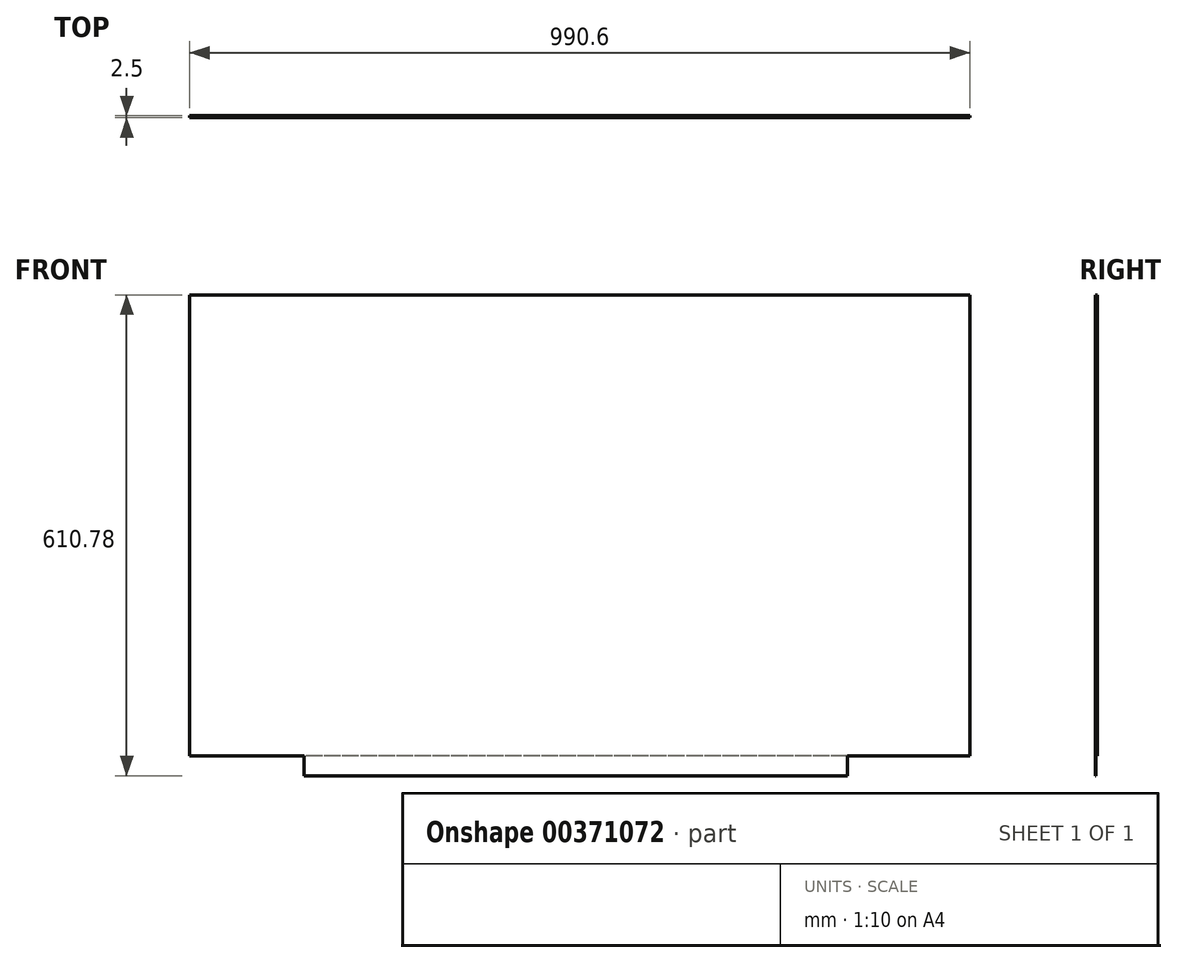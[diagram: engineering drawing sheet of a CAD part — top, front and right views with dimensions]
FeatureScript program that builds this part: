
annotation { "Feature Type Name" : "Feature", "Feature Type Description" : "" }
export const myFeature = defineFeature(function(context is Context, id is Id, definition is map)
    precondition{}
    {
        {
            var Q0;
            Q0=qCreatedBy(makeId("Front.planeOp"),FACE);
            var sketch = newSketch(context, id + "F0", { "sketchPlane" : qUnion([Q0])});
            skLineSegment(sketch, "E0.bottom", {"start": v(495.3, 292.9) * mm, "end": v(-495.3, 292.9) * mm});
            skLineSegment(sketch, "E0.top", {"start": v(495.3, -292.9) * mm, "end": v(-495.3, -292.9) * mm});
            skLineSegment(sketch, "E0.left", {"start": v(495.3, 292.9) * mm, "end": v(495.3, -292.9) * mm});
            skLineSegment(sketch, "E0.right", {"start": v(-495.3, 292.9) * mm, "end": v(-495.3, -292.9) * mm});
            skPoint(sketch, "E0.middle", {"position": v(0, 0) * mm});
            skSolve(sketch);
        }
        {
            var Q0;
            Q0=qSketchRegion(id+"F0",true);
            extrude(context, id + "F1", {"entities" : qUnion([Q0]), "depth" : 2.5 * mm});
        }
        {
            var Q0;
            Q0=makeQuery(id+"F1.opExtrude","CAP_FACE",FACE,{"disambiguationData":[OSD([sQuery(id+"F0.wireOp",EDGE,"E0.bottom"),sQuery(id+"F0.wireOp",EDGE,"E0.top"),sQuery(id+"F0.wireOp",EDGE,"E0.left"),sQuery(id+"F0.wireOp",EDGE,"E0.right")])],"isStart":false});
            var sketch = newSketch(context, id + "F2", { "sketchPlane" : qUnion([Q0])});
            skLineSegment(sketch, "E1.bottom", {"start": v(-350.3, -292.9) * mm, "end": v(340.3, -292.9) * mm});
            skLineSegment(sketch, "E1.top", {"start": v(-350.3, -317.9) * mm, "end": v(340.3, -317.9) * mm});
            skLineSegment(sketch, "E1.left", {"start": v(-350.3, -292.9) * mm, "end": v(-350.3, -317.9) * mm});
            skLineSegment(sketch, "E1.right", {"start": v(340.3, -292.9) * mm, "end": v(340.3, -317.9) * mm});
            skSolve(sketch);
        }
        {
            var Q0;
            Q0=qSketchRegion(id+"F2",true);
            extrude(context, id + "F3", {"entities" : qUnion([Q0]), "operationType" : NewBodyOperationType.ADD, "oppositeDirection" : true, "depth" : 0.5 * mm});
        }
    });
